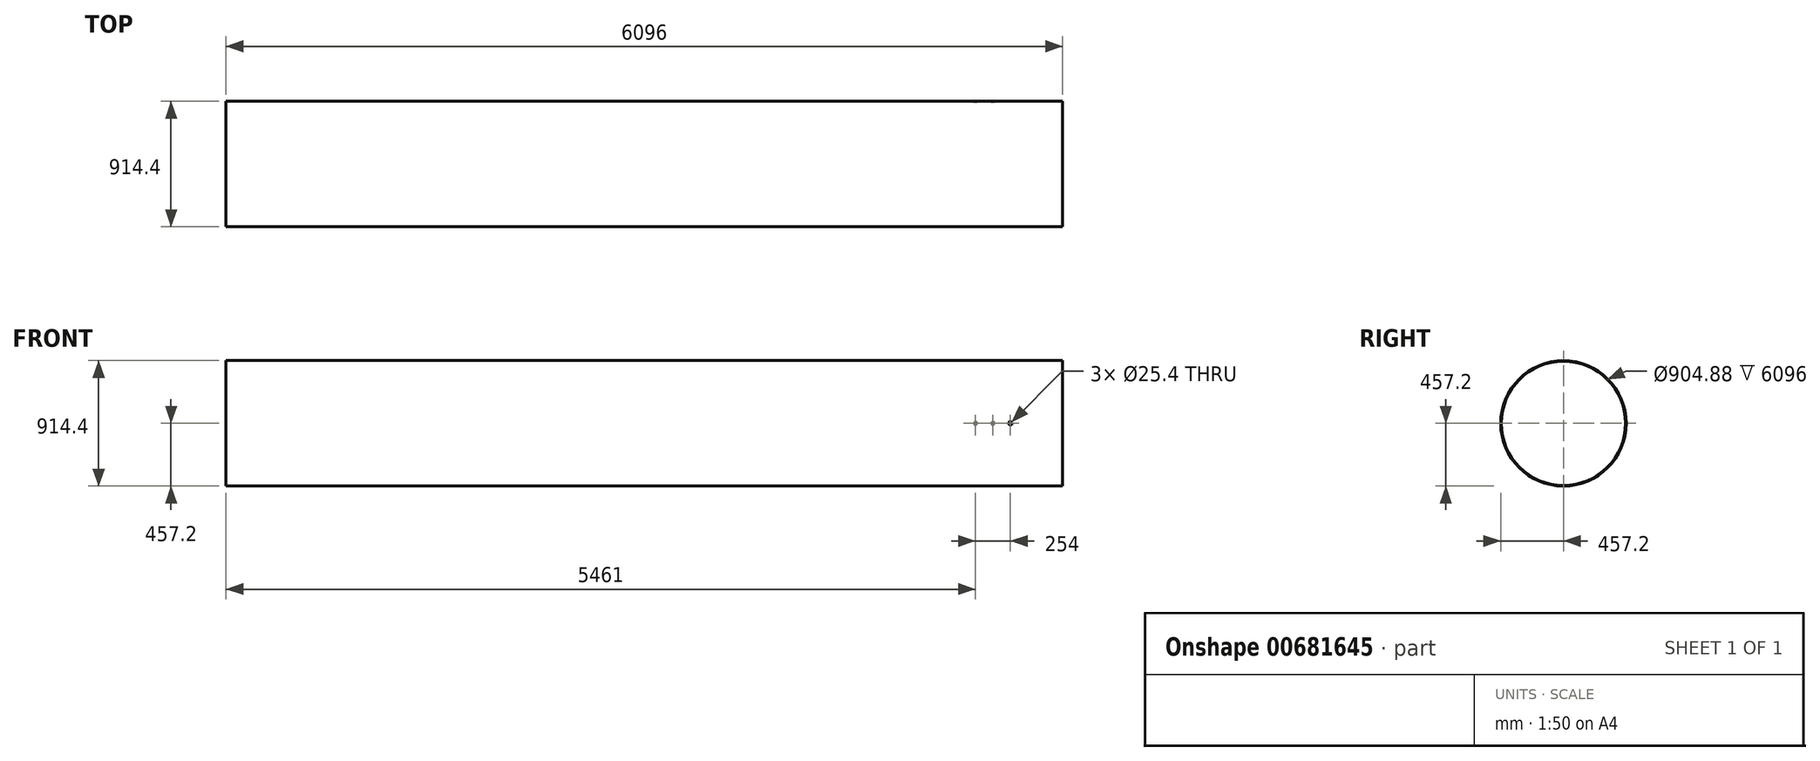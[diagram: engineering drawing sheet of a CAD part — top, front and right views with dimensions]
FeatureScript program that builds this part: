
annotation { "Feature Type Name" : "Feature", "Feature Type Description" : "" }
export const myFeature = defineFeature(function(context is Context, id is Id, definition is map)
    precondition{}
    {
        {
            var Q0;
            Q0=qCreatedBy(makeId("Right.planeOp"),FACE);
            var sketch = newSketch(context, id + "F0", { "sketchPlane" : qUnion([Q0])});
            skCircle(sketch, "E0", {"center": v(0, 0) * mm, "radius": 457.2 * mm});
            skCircle(sketch, "E1", {"center": v(0, 0) * mm, "radius": 452.44 * mm});
            skSolve(sketch);
        }
        {
            var Q0;
            Q0=makeQuery(id+"F0.imprint","IMPRINT",FACE,{"disambiguationData":[TD([[makeQuery(id+"F0.imprint","IMPRINT",EDGE,{"derivedFrom":sQuery(id+"F0.wireOp",EDGE,"E0")}),1.0]])]});
            extrude(context, id + "F1", {"entities" : qUnion([Q0]), "depth" : 6096 * mm, "offsetDistance" : 25.4 * mm});
        }
        {
            var Q0;
            Q0=qCreatedBy(makeId("Front.planeOp"),FACE);
            var sketch = newSketch(context, id + "F2", { "sketchPlane" : qUnion([Q0])});
            skLineSegment(sketch, "E2", {"start": v(0, 0) * mm, "end": v(5715, 0) * mm});
            skLineSegment(sketch, "E3", {"start": v(0, 0) * mm, "end": v(5588, 0) * mm});
            skLineSegment(sketch, "E4", {"start": v(0, 0) * mm, "end": v(5461, 0) * mm});
            skCircle(sketch, "E5", {"center": v(5461, 0) * mm, "radius": 12.7 * mm});
            skCircle(sketch, "E6", {"center": v(5588, 0) * mm, "radius": 12.7 * mm});
            skCircle(sketch, "E7", {"center": v(5715, 0) * mm, "radius": 12.7 * mm});
            skSolve(sketch);
        }
        {
            var Q0;
            {var subQ0=sQuery(id+"F2.wireOp",EDGE,"E4");var subQ1=sQuery(id+"F2.wireOp",EDGE,"E3");var subQ2=makeQuery(id+"F2.imprint","INTERSECT",VERTEX,{"derivedFrom":[subQ1,subQ0]});Q0=makeQuery(id+"F2.imprint","IMPRINT",FACE,{"disambiguationData":[TD([[makeQuery(id+"F2.imprint","IMPRINT",EDGE,{"disambiguationData":[TD([[subQ2,-1.0]])],"derivedFrom":subQ1}),1.0]])]});}
            var Q1;
            {var subQ0=sQuery(id+"F2.wireOp",EDGE,"E4");var subQ1=sQuery(id+"F2.wireOp",EDGE,"E3");var subQ2=makeQuery(id+"F2.imprint","INTERSECT",VERTEX,{"derivedFrom":[subQ1,subQ0]});Q1=makeQuery(id+"F2.imprint","IMPRINT",FACE,{"disambiguationData":[TD([[makeQuery(id+"F2.imprint","IMPRINT",EDGE,{"disambiguationData":[TD([[subQ2,-1.0]])],"derivedFrom":subQ1}),-1.0]])]});}
            var Q2;
            Q2=makeQuery(id+"F2.imprint","IMPRINT",FACE,{"disambiguationData":[TD([[makeQuery(id+"F2.imprint","IMPRINT",EDGE,{"derivedFrom":sQuery(id+"F2.wireOp",EDGE,"E7")}),1.0]])]});
            extrude(context, id + "F3", {"entities" : qUnion([Q0, Q1, Q2]), "operationType" : NewBodyOperationType.REMOVE, "depth" : 1216.15 * mm, "offsetDistance" : 25.4 * mm});
        }
        {
            var Q0;
            {var subQ0=sQuery(id+"F2.wireOp",EDGE,"E3");var subQ1=sQuery(id+"F2.wireOp",EDGE,"E2");var subQ2=makeQuery(id+"F2.imprint","INTERSECT",VERTEX,{"derivedFrom":[subQ1,subQ0]});Q0=makeQuery(id+"F2.imprint","IMPRINT",FACE,{"disambiguationData":[TD([[makeQuery(id+"F2.imprint","IMPRINT",EDGE,{"disambiguationData":[TD([[subQ2,-1.0]])],"derivedFrom":subQ1}),-1.0]])]});}
            var Q1;
            {var subQ0=sQuery(id+"F2.wireOp",EDGE,"E3");var subQ1=sQuery(id+"F2.wireOp",EDGE,"E2");var subQ2=makeQuery(id+"F2.imprint","INTERSECT",VERTEX,{"derivedFrom":[subQ1,subQ0]});Q1=makeQuery(id+"F2.imprint","IMPRINT",FACE,{"disambiguationData":[TD([[makeQuery(id+"F2.imprint","IMPRINT",EDGE,{"disambiguationData":[TD([[subQ2,-1.0]])],"derivedFrom":subQ1}),1.0]])]});}
            extrude(context, id + "F4", {"entities" : qUnion([Q0, Q1]), "operationType" : NewBodyOperationType.REMOVE, "oppositeDirection" : true, "depth" : 466.6 * mm, "offsetDistance" : 25.4 * mm});
        }
    });
